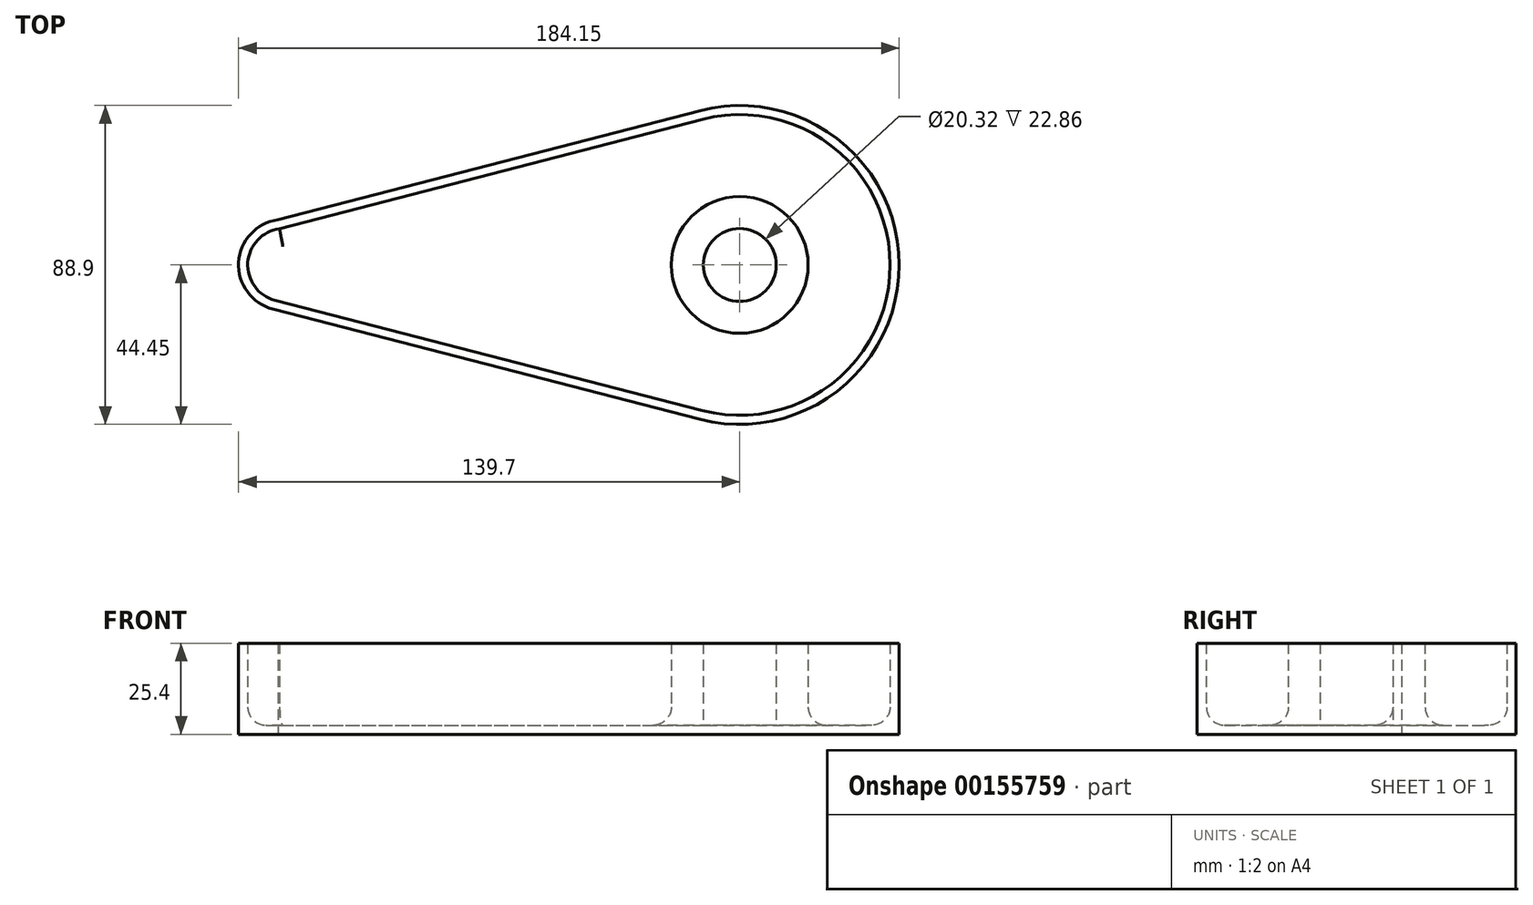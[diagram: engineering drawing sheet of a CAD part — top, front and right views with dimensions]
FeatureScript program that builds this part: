
annotation { "Feature Type Name" : "Feature", "Feature Type Description" : "" }
export const myFeature = defineFeature(function(context is Context, id is Id, definition is map)
    precondition{}
    {
        {
            var Q0;
            Q0=qCreatedBy(makeId("Top.planeOp"),FACE);
            var sketch = newSketch(context, id + "F0", { "sketchPlane" : qUnion([Q0])});
            skArc(sketch, "E0", {"start": v(-11.11, -43.04) * mm, "mid": v(44.45, 0.02) * mm, "end": v(-11.14, 43.03) * mm});
            skArc(sketch, "E1", {"start": v(-128.75, 12.58) * mm, "mid": v(-139.68, 0.73) * mm, "end": v(-130.18, -12.3) * mm});
            skLineSegment(sketch, "E2", {"start": v(-128.75, 12.58) * mm, "end": v(-11.14, 43.03) * mm});
            skLineSegment(sketch, "E3", {"start": v(-130.18, -12.3) * mm, "end": v(-11.11, -43.04) * mm});
            skSolve(sketch);
        }
        {
            var Q0;
            Q0=makeQuery(id+"F0.imprint","IMPRINT",FACE,{"disambiguationData":[TD([[makeQuery(id+"F0.imprint","IMPRINT",EDGE,{"derivedFrom":sQuery(id+"F0.wireOp",EDGE,"E0")}),1.0]])]});
            extrude(context, id + "F1", {"entities" : qUnion([Q0]), "depth" : 25.4 * mm});
        }
        {
            var Q0;
            Q0=makeQuery(id+"F1.opExtrude","CAP_FACE",FACE,{"disambiguationData":[OSD([sQuery(id+"F0.wireOp",EDGE,"E0"),sQuery(id+"F0.wireOp",EDGE,"E1"),sQuery(id+"F0.wireOp",EDGE,"E2"),sQuery(id+"F0.wireOp",EDGE,"E3")])],"isStart":false});
            shell(context, id + "F2", {"entities" : qUnion([Q0]), "thickness" : 2.54 * mm});
        }
        {
            var Q0;
            Q0=makeQuery(id+"F2.opShell","OFFSET_FACE",FACE,{"disambiguationData":[OSD([sQuery(id+"F0.wireOp",EDGE,"E0"),sQuery(id+"F0.wireOp",EDGE,"E1"),sQuery(id+"F0.wireOp",EDGE,"E2"),sQuery(id+"F0.wireOp",EDGE,"E3")])]});
            var sketch = newSketch(context, id + "F3", { "sketchPlane" : qUnion([Q0])});
            skCircle(sketch, "E4", {"center": v(0, 0) * mm, "radius": 19.05 * mm});
            skCircle(sketch, "E5", {"center": v(0, 0) * mm, "radius": 10.16 * mm});
            skSolve(sketch);
        }
        {
            var Q0;
            Q0=makeQuery(id+"F3.imprint","IMPRINT",FACE,{"disambiguationData":[TD([[makeQuery(id+"F3.imprint","IMPRINT",EDGE,{"derivedFrom":sQuery(id+"F3.wireOp",EDGE,"E4")}),1.0]])]});
            var Q1;
            Q1=makeQuery(id+"F1.opExtrude","CAP_FACE",FACE,{"disambiguationData":[OSD([sQuery(id+"F0.wireOp",EDGE,"E0"),sQuery(id+"F0.wireOp",EDGE,"E1"),sQuery(id+"F0.wireOp",EDGE,"E2"),sQuery(id+"F0.wireOp",EDGE,"E3")])],"isStart":false});
            extrude(context, id + "F4", {"entities" : qUnion([Q0]), "operationType" : NewBodyOperationType.ADD, "endBound" : BoundingType.UP_TO_SURFACE, "endBoundEntityFace" : qUnion([Q1]), "depth" : 25.4 * mm});
        }
        {
            var Q0;
            Q0=makeQuery(id+"F4.opExtrude","CAP_EDGE",EDGE,{"disambiguationData":[OSD([sQuery(id+"F3.wireOp",EDGE,"E4")])],"isStart":true});
            var Q1;
            {var subQ0=sQuery(id+"F0.wireOp",EDGE,"E3");var subQ1=sQuery(id+"F0.wireOp",EDGE,"E2");var subQ2=sQuery(id+"F0.wireOp",EDGE,"E1");var subQ3=sQuery(id+"F0.wireOp",EDGE,"E0");Q1=makeQuery(id+"F4.boolean.opBoolean","SPLIT",FACE,{"disambiguationData":[TD([makeQuery(id+"F2.opShell","OFFSET_FACE",FACE,{"disambiguationData":[OSD([subQ3])]})])],"derivedFrom":makeQuery(id+"F2.opShell","OFFSET_FACE",FACE,{"disambiguationData":[OSD([subQ3,subQ2,subQ1,subQ0])]})});}
            fillet(context, id + "F5", {"entities" : qUnion([Q0, Q1]), "radius" : 5.08 * mm, "tangentPropagation" : true, "allowEdgeOverflow" : false});
        }
    });
